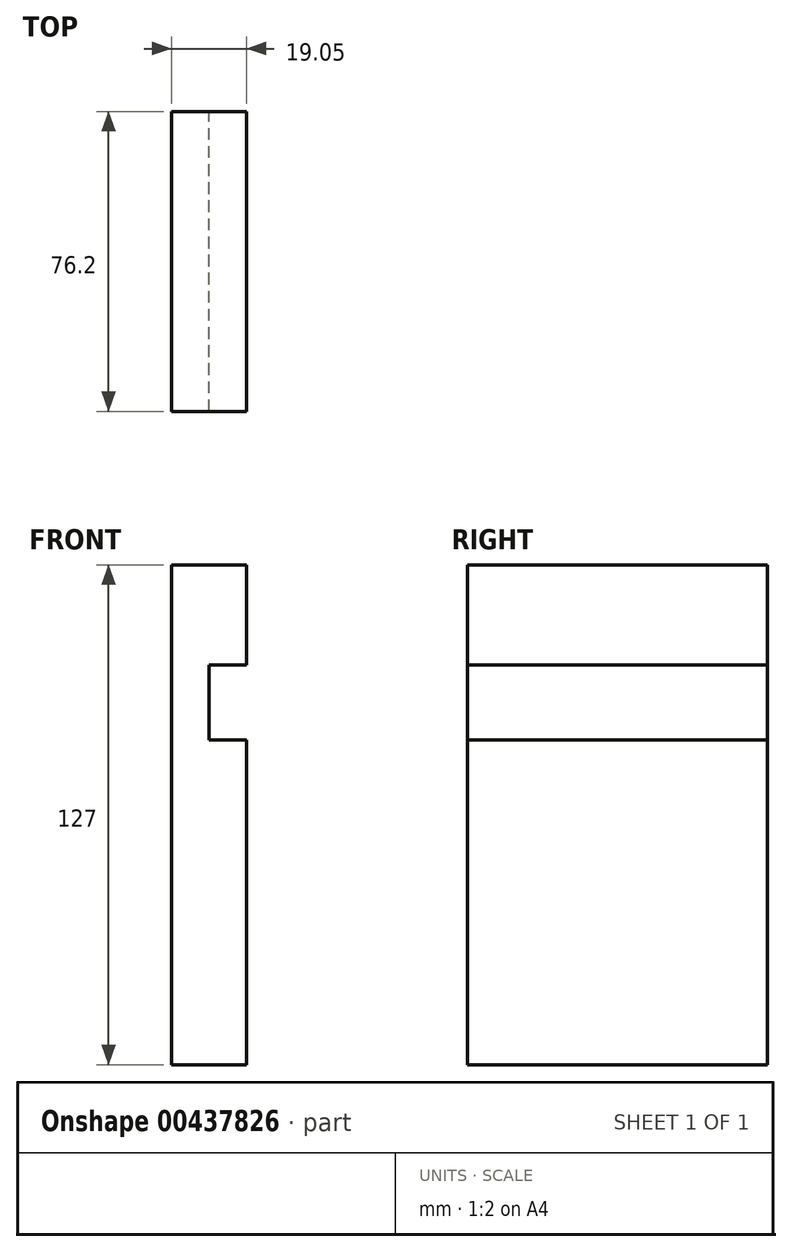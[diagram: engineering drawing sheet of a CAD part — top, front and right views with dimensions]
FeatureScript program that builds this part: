
annotation { "Feature Type Name" : "Feature", "Feature Type Description" : "" }
export const myFeature = defineFeature(function(context is Context, id is Id, definition is map)
    precondition{}
    {
        {
            var Q0;
            Q0=qCreatedBy(makeId("Front.planeOp"),FACE);
            var sketch = newSketch(context, id + "F0", { "sketchPlane" : qUnion([Q0])});
            skLineSegment(sketch, "E0", {"start": v(0, 59.2) * mm, "end": v(0, -67.8) * mm});
            skLineSegment(sketch, "E1", {"start": v(0, -67.8) * mm, "end": v(19.05, -67.8) * mm});
            skLineSegment(sketch, "E2", {"start": v(0, 59.2) * mm, "end": v(19.05, 59.2) * mm});
            skLineSegment(sketch, "E3", {"start": v(19.05, 33.8) * mm, "end": v(19.05, 59.2) * mm});
            skLineSegment(sketch, "E4", {"start": v(19.05, 33.8) * mm, "end": v(9.53, 33.8) * mm});
            skLineSegment(sketch, "E5", {"start": v(9.53, 33.8) * mm, "end": v(9.53, 14.75) * mm});
            skLineSegment(sketch, "E6", {"start": v(9.53, 14.75) * mm, "end": v(19.05, 14.75) * mm});
            skLineSegment(sketch, "E7", {"start": v(19.05, -67.8) * mm, "end": v(19.05, 14.75) * mm});
            skSolve(sketch);
        }
        {
            var Q0;
            Q0=makeQuery(id+"F0.imprint","IMPRINT",FACE,{"disambiguationData":[TD([[makeQuery(id+"F0.imprint","IMPRINT",EDGE,{"derivedFrom":sQuery(id+"F0.wireOp",EDGE,"E0")}),1.0]])]});
            extrude(context, id + "F1", {"entities" : qUnion([Q0]), "depth" : 76.2 * mm});
        }
    });
